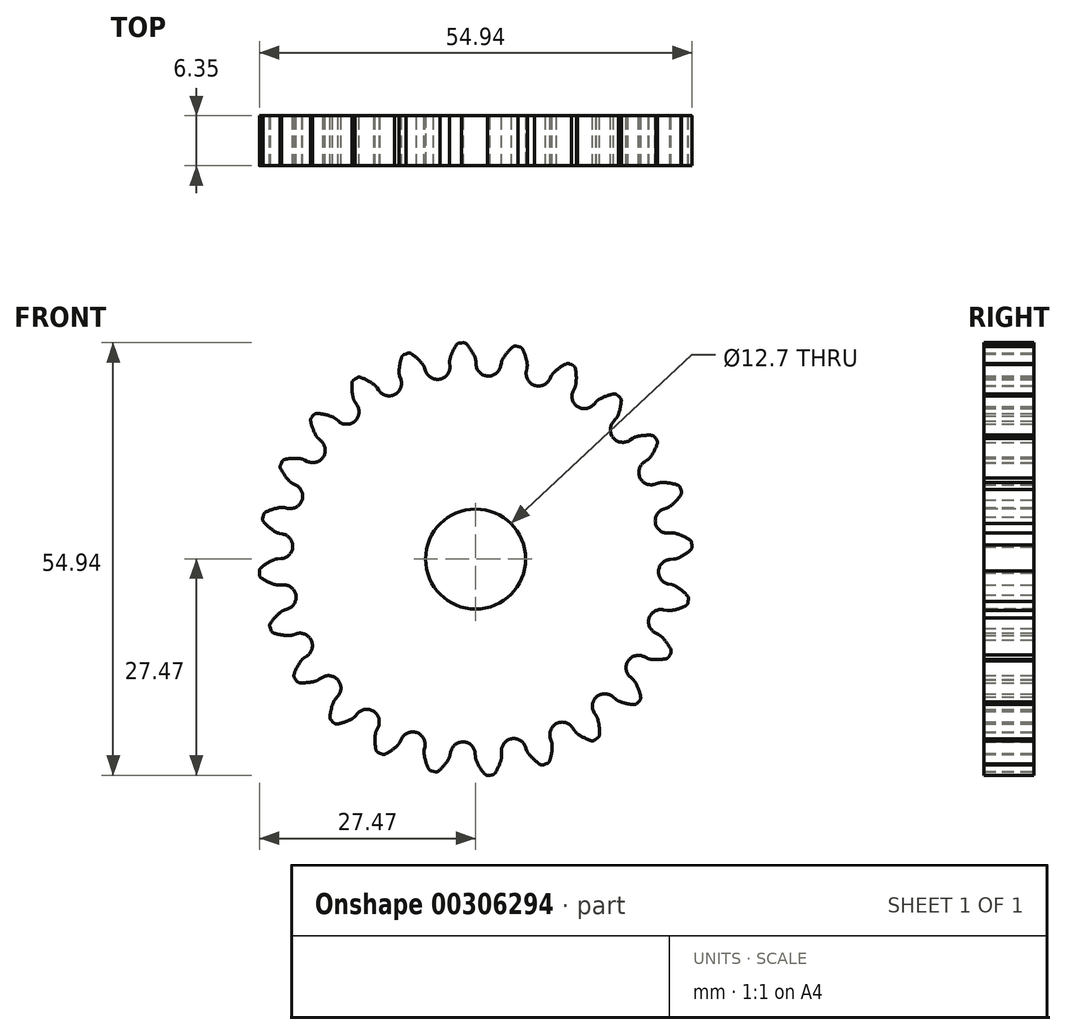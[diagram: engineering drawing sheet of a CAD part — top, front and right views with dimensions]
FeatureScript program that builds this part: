
annotation { "Feature Type Name" : "Feature", "Feature Type Description" : "" }
export const myFeature = defineFeature(function(context is Context, id is Id, definition is map)
    precondition{}
    {
        {
            var Q0;
            Q0=qCreatedBy(makeId("Front.planeOp"),FACE);
            var sketch = newSketch(context, id + "F0", { "sketchPlane" : qUnion([Q0])});
            skArc(sketch, "E0.trimOffspring", {"start": v(-0.1, 25.68) * mm, "mid": v(-0.56, 26.53) * mm, "end": v(-1.14, 27.3) * mm});
            skLineSegment(sketch, "E1", {"start": v(-1.55, 27.47) * mm, "end": v(-1.8, 27.46) * mm});
            skLineSegment(sketch, "E2.MirrorCS", {"start": v(-2.05, 27.44) * mm, "end": v(-1.8, 27.46) * mm});
            skArc(sketch, "E3.MirrorCS", {"start": v(-3.24, 25.47) * mm, "mid": v(-2.9, 26.38) * mm, "end": v(-2.43, 27.22) * mm});
            skLineSegment(sketch, "E4", {"start": v(0.02, 25.14) * mm, "end": v(0.05, 24.72) * mm});
            skLineSegment(sketch, "E5.MirrorCS", {"start": v(-3.3, 24.92) * mm, "end": v(-3.28, 24.5) * mm});
            skPoint(sketch, "E6.visualSharp", {"position": v(0.14, 23.28) * mm});
            skArc(sketch, "E6.filletArc", {"start": v(0.05, 24.72) * mm, "mid": v(0.51, 23.7) * mm, "end": v(1.54, 23.23) * mm});
            skPoint(sketch, "E7.visualSharp", {"position": v(-3.18, 23.06) * mm});
            skArc(sketch, "E7.filletArc", {"start": v(-4.56, 22.83) * mm, "mid": v(-3.6, 23.43) * mm, "end": v(-3.28, 24.5) * mm});
            skPoint(sketch, "E8.visualSharp", {"position": v(-3.32, 25.18) * mm});
            skArc(sketch, "E8.filletArc", {"start": v(-3.24, 25.47) * mm, "mid": v(-3.3, 25.2) * mm, "end": v(-3.3, 24.92) * mm});
            skPoint(sketch, "E9.visualSharp", {"position": v(0, 25.4) * mm});
            skArc(sketch, "E9.filletArc", {"start": v(0.02, 25.14) * mm, "mid": v(-0.02, 25.42) * mm, "end": v(-0.1, 25.68) * mm});
            skPoint(sketch, "E10.visualSharp", {"position": v(-2.3, 27.42) * mm});
            skArc(sketch, "E10.filletArc", {"start": v(-2.05, 27.44) * mm, "mid": v(-2.27, 27.37) * mm, "end": v(-2.43, 27.22) * mm});
            skPoint(sketch, "E11.visualSharp", {"position": v(-1.3, 27.49) * mm});
            skArc(sketch, "E11.filletArc", {"start": v(-1.14, 27.3) * mm, "mid": v(-1.32, 27.43) * mm, "end": v(-1.55, 27.47) * mm});
            skArc(sketch, "E12.1.0", {"start": v(-9.73, 23.77) * mm, "mid": v(-9.63, 24.73) * mm, "end": v(-9.4, 25.66) * mm});
            skPoint(sketch, "E12.1.1", {"position": v(-9.3, 25.9) * mm});
            skPoint(sketch, "E12.1.2", {"position": v(-8.38, 26.21) * mm});
            skArc(sketch, "E12.1.3", {"start": v(-10.31, 20.87) * mm, "mid": v(-9.54, 21.7) * mm, "end": v(-9.5, 22.82) * mm});
            skPoint(sketch, "E12.1.4", {"position": v(-5.89, 22.53) * mm});
            skPoint(sketch, "E12.1.5", {"position": v(-9.04, 21.46) * mm});
            skPoint(sketch, "E12.1.6", {"position": v(-9.73, 23.46) * mm});
            skArc(sketch, "E12.1.7", {"start": v(-6.35, 23.9) * mm, "mid": v(-5.64, 23.02) * mm, "end": v(-4.52, 22.84) * mm});
            skPoint(sketch, "E12.1.8", {"position": v(-6.57, 24.54) * mm});
            skArc(sketch, "E12.1.9", {"start": v(-6.75, 24.78) * mm, "mid": v(-7.41, 25.48) * mm, "end": v(-8.17, 26.08) * mm});
            skLineSegment(sketch, "E12.1.10", {"start": v(-9.64, 23.22) * mm, "end": v(-9.5, 22.82) * mm});
            skArc(sketch, "E12.1.11", {"start": v(-8.17, 26.08) * mm, "mid": v(-8.38, 26.16) * mm, "end": v(-8.6, 26.14) * mm});
            skArc(sketch, "E12.1.12", {"start": v(-6.48, 24.29) * mm, "mid": v(-6.6, 24.54) * mm, "end": v(-6.75, 24.78) * mm});
            skLineSegment(sketch, "E12.1.13", {"start": v(-6.48, 24.29) * mm, "end": v(-6.35, 23.9) * mm});
            skLineSegment(sketch, "E12.1.14", {"start": v(-8.6, 26.14) * mm, "end": v(-8.85, 26.06) * mm});
            skArc(sketch, "E12.1.15", {"start": v(-9.73, 23.77) * mm, "mid": v(-9.7, 23.49) * mm, "end": v(-9.64, 23.22) * mm});
            skLineSegment(sketch, "E12.1.16", {"start": v(-9.08, 25.97) * mm, "end": v(-8.85, 26.06) * mm});
            skArc(sketch, "E12.1.17", {"start": v(-9.08, 25.97) * mm, "mid": v(-9.28, 25.85) * mm, "end": v(-9.4, 25.66) * mm});
            skArc(sketch, "E12.2.0", {"start": v(-15.55, 20.44) * mm, "mid": v(-15.7, 21.4) * mm, "end": v(-15.71, 22.35) * mm});
            skPoint(sketch, "E12.2.1", {"position": v(-15.7, 22.6) * mm});
            skPoint(sketch, "E12.2.2", {"position": v(-14.88, 23.15) * mm});
            skArc(sketch, "E12.2.3", {"start": v(-15.37, 17.5) * mm, "mid": v(-14.83, 18.49) * mm, "end": v(-15.1, 19.58) * mm});
            skPoint(sketch, "E12.2.4", {"position": v(-11.52, 20.24) * mm});
            skPoint(sketch, "E12.2.5", {"position": v(-14.29, 18.38) * mm});
            skPoint(sketch, "E12.2.6", {"position": v(-15.47, 20.15) * mm});
            skArc(sketch, "E12.2.7", {"start": v(-12.32, 21.44) * mm, "mid": v(-11.4, 20.78) * mm, "end": v(-10.28, 20.9) * mm});
            skPoint(sketch, "E12.2.8", {"position": v(-12.7, 22) * mm});
            skArc(sketch, "E12.2.9", {"start": v(-12.93, 22.18) * mm, "mid": v(-13.75, 22.7) * mm, "end": v(-14.64, 23.07) * mm});
            skLineSegment(sketch, "E12.2.10", {"start": v(-15.32, 19.93) * mm, "end": v(-15.1, 19.58) * mm});
            skArc(sketch, "E12.2.11", {"start": v(-14.64, 23.07) * mm, "mid": v(-14.86, 23.1) * mm, "end": v(-15.08, 23.02) * mm});
            skArc(sketch, "E12.2.12", {"start": v(-12.55, 21.78) * mm, "mid": v(-12.72, 22) * mm, "end": v(-12.93, 22.18) * mm});
            skLineSegment(sketch, "E12.2.13", {"start": v(-12.55, 21.78) * mm, "end": v(-12.32, 21.44) * mm});
            skLineSegment(sketch, "E12.2.14", {"start": v(-15.08, 23.02) * mm, "end": v(-15.29, 22.88) * mm});
            skArc(sketch, "E12.2.15", {"start": v(-15.55, 20.44) * mm, "mid": v(-15.46, 20.18) * mm, "end": v(-15.32, 19.93) * mm});
            skLineSegment(sketch, "E12.2.16", {"start": v(-15.5, 22.74) * mm, "end": v(-15.29, 22.88) * mm});
            skArc(sketch, "E12.2.17", {"start": v(-15.5, 22.74) * mm, "mid": v(-15.65, 22.57) * mm, "end": v(-15.71, 22.35) * mm});
            skPoint(sketch, "E12.center", {"position": v(0, 0) * mm});
            skPoint(sketch, "E13.4.3.0", {"position": v(-21, 17.77) * mm});
            skPoint(sketch, "E13.5.3.0", {"position": v(-20.36, 18.51) * mm});
            skArc(sketch, "E13.6.3.0", {"start": v(-19.37, 12.92) * mm, "mid": v(-19.11, 14.02) * mm, "end": v(-19.65, 15.01) * mm});
            skPoint(sketch, "E13.10.3.0", {"position": v(-16.36, 16.57) * mm});
            skPoint(sketch, "E13.11.3.0", {"position": v(-18.56, 14.06) * mm});
            skPoint(sketch, "E13.12.3.0", {"position": v(-20.15, 15.46) * mm});
            skArc(sketch, "E13.13.3.0", {"start": v(-17.45, 17.52) * mm, "mid": v(-16.4, 17.12) * mm, "end": v(-15.34, 17.52) * mm});
            skPoint(sketch, "E13.17.3.0", {"position": v(-17.96, 17.96) * mm});
            skArc(sketch, "E13.18.3.0", {"start": v(-18.24, 18.08) * mm, "mid": v(-19.16, 18.36) * mm, "end": v(-20.11, 18.5) * mm});
            skArc(sketch, "E13.19.3.0", {"start": v(-20.3, 15.72) * mm, "mid": v(-20.7, 16.6) * mm, "end": v(-20.97, 17.52) * mm});
            skLineSegment(sketch, "E13.22.3.0", {"start": v(-19.96, 15.29) * mm, "end": v(-19.65, 15.01) * mm});
            skArc(sketch, "E13.25.3.0", {"start": v(-20.11, 18.5) * mm, "mid": v(-20.34, 18.46) * mm, "end": v(-20.52, 18.33) * mm});
            skArc(sketch, "E13.29.3.0", {"start": v(-17.76, 17.8) * mm, "mid": v(-17.99, 17.96) * mm, "end": v(-18.24, 18.08) * mm});
            skLineSegment(sketch, "E13.33.3.0", {"start": v(-17.76, 17.8) * mm, "end": v(-17.45, 17.52) * mm});
            skLineSegment(sketch, "E13.36.3.0", {"start": v(-20.52, 18.33) * mm, "end": v(-20.7, 18.15) * mm});
            skArc(sketch, "E13.39.3.0", {"start": v(-20.3, 15.72) * mm, "mid": v(-20.15, 15.49) * mm, "end": v(-19.96, 15.29) * mm});
            skLineSegment(sketch, "E13.43.3.0", {"start": v(-20.85, 17.95) * mm, "end": v(-20.7, 18.15) * mm});
            skArc(sketch, "E13.46.3.0", {"start": v(-20.85, 17.95) * mm, "mid": v(-20.96, 17.75) * mm, "end": v(-20.97, 17.52) * mm});
            skPoint(sketch, "E13.4.4.0", {"position": v(-24.9, 11.73) * mm});
            skPoint(sketch, "E13.5.4.0", {"position": v(-24.46, 12.6) * mm});
            skArc(sketch, "E13.6.4.0", {"start": v(-22.05, 7.47) * mm, "mid": v(-22.1, 8.6) * mm, "end": v(-22.86, 9.42) * mm});
            skPoint(sketch, "E13.10.4.0", {"position": v(-20.1, 11.77) * mm});
            skPoint(sketch, "E13.11.4.0", {"position": v(-21.57, 8.78) * mm});
            skPoint(sketch, "E13.12.4.0", {"position": v(-23.47, 9.71) * mm});
            skArc(sketch, "E13.13.4.0", {"start": v(-21.39, 12.4) * mm, "mid": v(-20.27, 12.3) * mm, "end": v(-19.35, 12.95) * mm});
            skPoint(sketch, "E13.17.4.0", {"position": v(-22, 12.7) * mm});
            skArc(sketch, "E13.18.4.0", {"start": v(-22.3, 12.74) * mm, "mid": v(-23.26, 12.78) * mm, "end": v(-24.21, 12.66) * mm});
            skArc(sketch, "E13.19.4.0", {"start": v(-23.68, 9.93) * mm, "mid": v(-24.3, 10.67) * mm, "end": v(-24.79, 11.5) * mm});
            skLineSegment(sketch, "E13.22.4.0", {"start": v(-23.23, 9.6) * mm, "end": v(-22.86, 9.42) * mm});
            skArc(sketch, "E13.25.4.0", {"start": v(-24.21, 12.66) * mm, "mid": v(-24.42, 12.57) * mm, "end": v(-24.57, 12.4) * mm});
            skArc(sketch, "E13.29.4.0", {"start": v(-21.76, 12.59) * mm, "mid": v(-22.02, 12.7) * mm, "end": v(-22.3, 12.74) * mm});
            skLineSegment(sketch, "E13.33.4.0", {"start": v(-21.76, 12.59) * mm, "end": v(-21.39, 12.4) * mm});
            skLineSegment(sketch, "E13.36.4.0", {"start": v(-24.57, 12.4) * mm, "end": v(-24.68, 12.17) * mm});
            skArc(sketch, "E13.39.4.0", {"start": v(-23.68, 9.93) * mm, "mid": v(-23.47, 9.74) * mm, "end": v(-23.23, 9.6) * mm});
            skLineSegment(sketch, "E13.43.4.0", {"start": v(-24.8, 11.94) * mm, "end": v(-24.68, 12.17) * mm});
            skArc(sketch, "E13.46.4.0", {"start": v(-24.8, 11.94) * mm, "mid": v(-24.84, 11.72) * mm, "end": v(-24.79, 11.5) * mm});
            skPoint(sketch, "E13.4.5.0", {"position": v(-27.08, 4.88) * mm});
            skPoint(sketch, "E13.5.5.0", {"position": v(-26.89, 5.85) * mm});
            skArc(sketch, "E13.6.5.0", {"start": v(-23.23, 1.5) * mm, "mid": v(-23.56, 2.58) * mm, "end": v(-24.52, 3.18) * mm});
            skPoint(sketch, "E13.10.5.0", {"position": v(-22.45, 6.17) * mm});
            skPoint(sketch, "E13.11.5.0", {"position": v(-23.1, 2.9) * mm});
            skPoint(sketch, "E13.12.5.0", {"position": v(-25.18, 3.3) * mm});
            skArc(sketch, "E13.13.5.0", {"start": v(-23.87, 6.45) * mm, "mid": v(-22.76, 6.63) * mm, "end": v(-22.04, 7.5) * mm});
            skPoint(sketch, "E13.17.5.0", {"position": v(-24.53, 6.58) * mm});
            skArc(sketch, "E13.18.5.0", {"start": v(-24.83, 6.54) * mm, "mid": v(-25.77, 6.32) * mm, "end": v(-26.67, 5.96) * mm});
            skArc(sketch, "E13.19.5.0", {"start": v(-25.45, 3.46) * mm, "mid": v(-26.23, 4.02) * mm, "end": v(-26.92, 4.7) * mm});
            skLineSegment(sketch, "E13.22.5.0", {"start": v(-24.93, 3.26) * mm, "end": v(-24.52, 3.18) * mm});
            skArc(sketch, "E13.25.5.0", {"start": v(-26.67, 5.96) * mm, "mid": v(-26.84, 5.82) * mm, "end": v(-26.94, 5.62) * mm});
            skArc(sketch, "E13.29.5.0", {"start": v(-24.28, 6.53) * mm, "mid": v(-24.55, 6.56) * mm, "end": v(-24.83, 6.54) * mm});
            skLineSegment(sketch, "E13.33.5.0", {"start": v(-24.28, 6.53) * mm, "end": v(-23.87, 6.45) * mm});
            skLineSegment(sketch, "E13.36.5.0", {"start": v(-26.94, 5.62) * mm, "end": v(-27, 5.37) * mm});
            skArc(sketch, "E13.39.5.0", {"start": v(-25.45, 3.46) * mm, "mid": v(-25.2, 3.34) * mm, "end": v(-24.93, 3.26) * mm});
            skLineSegment(sketch, "E13.43.5.0", {"start": v(-27.04, 5.12) * mm, "end": v(-27, 5.37) * mm});
            skArc(sketch, "E13.46.5.0", {"start": v(-27.04, 5.12) * mm, "mid": v(-27.03, 4.9) * mm, "end": v(-26.92, 4.7) * mm});
            skPoint(sketch, "E13.4.6.0", {"position": v(-27.42, -2.3) * mm});
            skPoint(sketch, "E13.5.6.0", {"position": v(-27.49, -1.3) * mm});
            skArc(sketch, "E13.6.6.0", {"start": v(-22.83, -4.56) * mm, "mid": v(-23.43, -3.6) * mm, "end": v(-24.5, -3.28) * mm});
            skPoint(sketch, "E13.10.6.0", {"position": v(-23.28, 0.14) * mm});
            skPoint(sketch, "E13.11.6.0", {"position": v(-23.06, -3.18) * mm});
            skPoint(sketch, "E13.12.6.0", {"position": v(-25.18, -3.32) * mm});
            skArc(sketch, "E13.13.6.0", {"start": v(-24.72, 0.05) * mm, "mid": v(-23.7, 0.51) * mm, "end": v(-23.23, 1.54) * mm});
            skPoint(sketch, "E13.17.6.0", {"position": v(-25.4, 0) * mm});
            skArc(sketch, "E13.18.6.0", {"start": v(-25.68, -0.1) * mm, "mid": v(-26.53, -0.56) * mm, "end": v(-27.3, -1.14) * mm});
            skArc(sketch, "E13.19.6.0", {"start": v(-25.47, -3.24) * mm, "mid": v(-26.38, -2.9) * mm, "end": v(-27.22, -2.43) * mm});
            skLineSegment(sketch, "E13.22.6.0", {"start": v(-24.92, -3.3) * mm, "end": v(-24.5, -3.28) * mm});
            skArc(sketch, "E13.25.6.0", {"start": v(-27.3, -1.14) * mm, "mid": v(-27.43, -1.32) * mm, "end": v(-27.47, -1.55) * mm});
            skArc(sketch, "E13.29.6.0", {"start": v(-25.14, 0.02) * mm, "mid": v(-25.42, -0.02) * mm, "end": v(-25.68, -0.1) * mm});
            skLineSegment(sketch, "E13.33.6.0", {"start": v(-25.14, 0.02) * mm, "end": v(-24.72, 0.05) * mm});
            skLineSegment(sketch, "E13.36.6.0", {"start": v(-27.47, -1.55) * mm, "end": v(-27.46, -1.8) * mm});
            skArc(sketch, "E13.39.6.0", {"start": v(-25.47, -3.24) * mm, "mid": v(-25.2, -3.3) * mm, "end": v(-24.92, -3.3) * mm});
            skLineSegment(sketch, "E13.43.6.0", {"start": v(-27.44, -2.05) * mm, "end": v(-27.46, -1.8) * mm});
            skArc(sketch, "E13.46.6.0", {"start": v(-27.44, -2.05) * mm, "mid": v(-27.37, -2.27) * mm, "end": v(-27.22, -2.43) * mm});
            skPoint(sketch, "E13.4.7.0", {"position": v(-25.9, -9.3) * mm});
            skPoint(sketch, "E13.5.7.0", {"position": v(-26.21, -8.38) * mm});
            skArc(sketch, "E13.6.7.0", {"start": v(-20.87, -10.31) * mm, "mid": v(-21.7, -9.54) * mm, "end": v(-22.82, -9.5) * mm});
            skPoint(sketch, "E13.10.7.0", {"position": v(-22.53, -5.89) * mm});
            skPoint(sketch, "E13.11.7.0", {"position": v(-21.46, -9.04) * mm});
            skPoint(sketch, "E13.12.7.0", {"position": v(-23.46, -9.73) * mm});
            skArc(sketch, "E13.13.7.0", {"start": v(-23.9, -6.35) * mm, "mid": v(-23.02, -5.64) * mm, "end": v(-22.84, -4.52) * mm});
            skPoint(sketch, "E13.17.7.0", {"position": v(-24.54, -6.57) * mm});
            skArc(sketch, "E13.18.7.0", {"start": v(-24.78, -6.75) * mm, "mid": v(-25.48, -7.41) * mm, "end": v(-26.08, -8.17) * mm});
            skArc(sketch, "E13.19.7.0", {"start": v(-23.77, -9.73) * mm, "mid": v(-24.73, -9.63) * mm, "end": v(-25.66, -9.4) * mm});
            skLineSegment(sketch, "E13.22.7.0", {"start": v(-23.22, -9.64) * mm, "end": v(-22.82, -9.5) * mm});
            skArc(sketch, "E13.25.7.0", {"start": v(-26.08, -8.17) * mm, "mid": v(-26.16, -8.38) * mm, "end": v(-26.14, -8.6) * mm});
            skArc(sketch, "E13.29.7.0", {"start": v(-24.29, -6.48) * mm, "mid": v(-24.54, -6.6) * mm, "end": v(-24.78, -6.75) * mm});
            skLineSegment(sketch, "E13.33.7.0", {"start": v(-24.29, -6.48) * mm, "end": v(-23.9, -6.35) * mm});
            skLineSegment(sketch, "E13.36.7.0", {"start": v(-26.14, -8.6) * mm, "end": v(-26.06, -8.85) * mm});
            skArc(sketch, "E13.39.7.0", {"start": v(-23.77, -9.73) * mm, "mid": v(-23.49, -9.7) * mm, "end": v(-23.22, -9.64) * mm});
            skLineSegment(sketch, "E13.43.7.0", {"start": v(-25.97, -9.08) * mm, "end": v(-26.06, -8.85) * mm});
            skArc(sketch, "E13.46.7.0", {"start": v(-25.97, -9.08) * mm, "mid": v(-25.85, -9.28) * mm, "end": v(-25.66, -9.4) * mm});
            skPoint(sketch, "E13.4.8.0", {"position": v(-22.6, -15.7) * mm});
            skPoint(sketch, "E13.5.8.0", {"position": v(-23.15, -14.88) * mm});
            skArc(sketch, "E13.6.8.0", {"start": v(-17.5, -15.37) * mm, "mid": v(-18.49, -14.83) * mm, "end": v(-19.58, -15.1) * mm});
            skPoint(sketch, "E13.10.8.0", {"position": v(-20.24, -11.52) * mm});
            skPoint(sketch, "E13.11.8.0", {"position": v(-18.38, -14.29) * mm});
            skPoint(sketch, "E13.12.8.0", {"position": v(-20.15, -15.47) * mm});
            skArc(sketch, "E13.13.8.0", {"start": v(-21.44, -12.32) * mm, "mid": v(-20.78, -11.4) * mm, "end": v(-20.9, -10.28) * mm});
            skPoint(sketch, "E13.17.8.0", {"position": v(-22, -12.7) * mm});
            skArc(sketch, "E13.18.8.0", {"start": v(-22.18, -12.93) * mm, "mid": v(-22.7, -13.75) * mm, "end": v(-23.07, -14.64) * mm});
            skArc(sketch, "E13.19.8.0", {"start": v(-20.44, -15.55) * mm, "mid": v(-21.4, -15.7) * mm, "end": v(-22.35, -15.71) * mm});
            skLineSegment(sketch, "E13.22.8.0", {"start": v(-19.93, -15.32) * mm, "end": v(-19.58, -15.1) * mm});
            skArc(sketch, "E13.25.8.0", {"start": v(-23.07, -14.64) * mm, "mid": v(-23.1, -14.86) * mm, "end": v(-23.02, -15.08) * mm});
            skArc(sketch, "E13.29.8.0", {"start": v(-21.78, -12.55) * mm, "mid": v(-22, -12.72) * mm, "end": v(-22.18, -12.93) * mm});
            skLineSegment(sketch, "E13.33.8.0", {"start": v(-21.78, -12.55) * mm, "end": v(-21.44, -12.32) * mm});
            skLineSegment(sketch, "E13.36.8.0", {"start": v(-23.02, -15.08) * mm, "end": v(-22.88, -15.29) * mm});
            skArc(sketch, "E13.39.8.0", {"start": v(-20.44, -15.55) * mm, "mid": v(-20.18, -15.46) * mm, "end": v(-19.93, -15.32) * mm});
            skLineSegment(sketch, "E13.43.8.0", {"start": v(-22.74, -15.5) * mm, "end": v(-22.88, -15.29) * mm});
            skArc(sketch, "E13.46.8.0", {"start": v(-22.74, -15.5) * mm, "mid": v(-22.57, -15.65) * mm, "end": v(-22.35, -15.71) * mm});
            skPoint(sketch, "E13.4.9.0", {"position": v(-17.77, -21) * mm});
            skPoint(sketch, "E13.5.9.0", {"position": v(-18.51, -20.36) * mm});
            skArc(sketch, "E13.6.9.0", {"start": v(-12.92, -19.37) * mm, "mid": v(-14.02, -19.11) * mm, "end": v(-15.01, -19.65) * mm});
            skPoint(sketch, "E13.10.9.0", {"position": v(-16.57, -16.36) * mm});
            skPoint(sketch, "E13.11.9.0", {"position": v(-14.06, -18.56) * mm});
            skPoint(sketch, "E13.12.9.0", {"position": v(-15.46, -20.15) * mm});
            skArc(sketch, "E13.13.9.0", {"start": v(-17.52, -17.45) * mm, "mid": v(-17.12, -16.4) * mm, "end": v(-17.52, -15.34) * mm});
            skPoint(sketch, "E13.17.9.0", {"position": v(-17.96, -17.96) * mm});
            skArc(sketch, "E13.18.9.0", {"start": v(-18.08, -18.24) * mm, "mid": v(-18.36, -19.16) * mm, "end": v(-18.5, -20.11) * mm});
            skArc(sketch, "E13.19.9.0", {"start": v(-15.72, -20.3) * mm, "mid": v(-16.6, -20.7) * mm, "end": v(-17.52, -20.97) * mm});
            skLineSegment(sketch, "E13.22.9.0", {"start": v(-15.29, -19.96) * mm, "end": v(-15.01, -19.65) * mm});
            skArc(sketch, "E13.25.9.0", {"start": v(-18.5, -20.11) * mm, "mid": v(-18.46, -20.34) * mm, "end": v(-18.33, -20.52) * mm});
            skArc(sketch, "E13.29.9.0", {"start": v(-17.8, -17.76) * mm, "mid": v(-17.96, -17.99) * mm, "end": v(-18.08, -18.24) * mm});
            skLineSegment(sketch, "E13.33.9.0", {"start": v(-17.8, -17.76) * mm, "end": v(-17.52, -17.45) * mm});
            skLineSegment(sketch, "E13.36.9.0", {"start": v(-18.33, -20.52) * mm, "end": v(-18.15, -20.7) * mm});
            skArc(sketch, "E13.39.9.0", {"start": v(-15.72, -20.3) * mm, "mid": v(-15.49, -20.15) * mm, "end": v(-15.29, -19.96) * mm});
            skLineSegment(sketch, "E13.43.9.0", {"start": v(-17.95, -20.85) * mm, "end": v(-18.15, -20.7) * mm});
            skArc(sketch, "E13.46.9.0", {"start": v(-17.95, -20.85) * mm, "mid": v(-17.75, -20.96) * mm, "end": v(-17.52, -20.97) * mm});
            skPoint(sketch, "E13.4.10.0", {"position": v(-11.73, -24.9) * mm});
            skPoint(sketch, "E13.5.10.0", {"position": v(-12.6, -24.46) * mm});
            skArc(sketch, "E13.6.10.0", {"start": v(-7.47, -22.05) * mm, "mid": v(-8.6, -22.1) * mm, "end": v(-9.42, -22.86) * mm});
            skPoint(sketch, "E13.10.10.0", {"position": v(-11.77, -20.1) * mm});
            skPoint(sketch, "E13.11.10.0", {"position": v(-8.78, -21.57) * mm});
            skPoint(sketch, "E13.12.10.0", {"position": v(-9.71, -23.47) * mm});
            skArc(sketch, "E13.13.10.0", {"start": v(-12.4, -21.39) * mm, "mid": v(-12.3, -20.27) * mm, "end": v(-12.95, -19.35) * mm});
            skPoint(sketch, "E13.17.10.0", {"position": v(-12.7, -22) * mm});
            skArc(sketch, "E13.18.10.0", {"start": v(-12.74, -22.3) * mm, "mid": v(-12.78, -23.26) * mm, "end": v(-12.66, -24.21) * mm});
            skArc(sketch, "E13.19.10.0", {"start": v(-9.93, -23.68) * mm, "mid": v(-10.67, -24.3) * mm, "end": v(-11.5, -24.79) * mm});
            skLineSegment(sketch, "E13.22.10.0", {"start": v(-9.6, -23.23) * mm, "end": v(-9.42, -22.86) * mm});
            skArc(sketch, "E13.25.10.0", {"start": v(-12.66, -24.21) * mm, "mid": v(-12.57, -24.42) * mm, "end": v(-12.4, -24.57) * mm});
            skArc(sketch, "E13.29.10.0", {"start": v(-12.59, -21.76) * mm, "mid": v(-12.7, -22.02) * mm, "end": v(-12.74, -22.3) * mm});
            skLineSegment(sketch, "E13.33.10.0", {"start": v(-12.59, -21.76) * mm, "end": v(-12.4, -21.39) * mm});
            skLineSegment(sketch, "E13.36.10.0", {"start": v(-12.4, -24.57) * mm, "end": v(-12.17, -24.68) * mm});
            skArc(sketch, "E13.39.10.0", {"start": v(-9.93, -23.68) * mm, "mid": v(-9.74, -23.47) * mm, "end": v(-9.6, -23.23) * mm});
            skLineSegment(sketch, "E13.43.10.0", {"start": v(-11.94, -24.8) * mm, "end": v(-12.17, -24.68) * mm});
            skArc(sketch, "E13.46.10.0", {"start": v(-11.94, -24.8) * mm, "mid": v(-11.72, -24.84) * mm, "end": v(-11.5, -24.79) * mm});
            skPoint(sketch, "E13.4.11.0", {"position": v(-4.88, -27.08) * mm});
            skPoint(sketch, "E13.5.11.0", {"position": v(-5.85, -26.89) * mm});
            skArc(sketch, "E13.6.11.0", {"start": v(-1.5, -23.23) * mm, "mid": v(-2.58, -23.56) * mm, "end": v(-3.18, -24.52) * mm});
            skPoint(sketch, "E13.10.11.0", {"position": v(-6.17, -22.45) * mm});
            skPoint(sketch, "E13.11.11.0", {"position": v(-2.9, -23.1) * mm});
            skPoint(sketch, "E13.12.11.0", {"position": v(-3.3, -25.18) * mm});
            skArc(sketch, "E13.13.11.0", {"start": v(-6.45, -23.87) * mm, "mid": v(-6.63, -22.76) * mm, "end": v(-7.5, -22.04) * mm});
            skPoint(sketch, "E13.17.11.0", {"position": v(-6.58, -24.53) * mm});
            skArc(sketch, "E13.18.11.0", {"start": v(-6.54, -24.83) * mm, "mid": v(-6.32, -25.77) * mm, "end": v(-5.96, -26.67) * mm});
            skArc(sketch, "E13.19.11.0", {"start": v(-3.46, -25.45) * mm, "mid": v(-4.02, -26.23) * mm, "end": v(-4.7, -26.92) * mm});
            skLineSegment(sketch, "E13.22.11.0", {"start": v(-3.26, -24.93) * mm, "end": v(-3.18, -24.52) * mm});
            skArc(sketch, "E13.25.11.0", {"start": v(-5.96, -26.67) * mm, "mid": v(-5.82, -26.84) * mm, "end": v(-5.62, -26.94) * mm});
            skArc(sketch, "E13.29.11.0", {"start": v(-6.53, -24.28) * mm, "mid": v(-6.56, -24.55) * mm, "end": v(-6.54, -24.83) * mm});
            skLineSegment(sketch, "E13.33.11.0", {"start": v(-6.53, -24.28) * mm, "end": v(-6.45, -23.87) * mm});
            skLineSegment(sketch, "E13.36.11.0", {"start": v(-5.62, -26.94) * mm, "end": v(-5.37, -27) * mm});
            skArc(sketch, "E13.39.11.0", {"start": v(-3.46, -25.45) * mm, "mid": v(-3.34, -25.2) * mm, "end": v(-3.26, -24.93) * mm});
            skLineSegment(sketch, "E13.43.11.0", {"start": v(-5.12, -27.04) * mm, "end": v(-5.37, -27) * mm});
            skArc(sketch, "E13.46.11.0", {"start": v(-5.12, -27.04) * mm, "mid": v(-4.9, -27.03) * mm, "end": v(-4.7, -26.92) * mm});
            skPoint(sketch, "E13.4.12.0", {"position": v(2.3, -27.42) * mm});
            skPoint(sketch, "E13.5.12.0", {"position": v(1.3, -27.49) * mm});
            skArc(sketch, "E13.6.12.0", {"start": v(4.56, -22.83) * mm, "mid": v(3.6, -23.43) * mm, "end": v(3.28, -24.5) * mm});
            skPoint(sketch, "E13.10.12.0", {"position": v(-0.14, -23.28) * mm});
            skPoint(sketch, "E13.11.12.0", {"position": v(3.18, -23.06) * mm});
            skPoint(sketch, "E13.12.12.0", {"position": v(3.32, -25.18) * mm});
            skArc(sketch, "E13.13.12.0", {"start": v(-0.05, -24.72) * mm, "mid": v(-0.51, -23.7) * mm, "end": v(-1.54, -23.23) * mm});
            skPoint(sketch, "E13.17.12.0", {"position": v(0, -25.4) * mm});
            skArc(sketch, "E13.18.12.0", {"start": v(0.1, -25.68) * mm, "mid": v(0.56, -26.53) * mm, "end": v(1.14, -27.3) * mm});
            skArc(sketch, "E13.19.12.0", {"start": v(3.24, -25.47) * mm, "mid": v(2.9, -26.38) * mm, "end": v(2.43, -27.22) * mm});
            skLineSegment(sketch, "E13.22.12.0", {"start": v(3.3, -24.92) * mm, "end": v(3.28, -24.5) * mm});
            skArc(sketch, "E13.25.12.0", {"start": v(1.14, -27.3) * mm, "mid": v(1.32, -27.43) * mm, "end": v(1.55, -27.47) * mm});
            skArc(sketch, "E13.29.12.0", {"start": v(-0.02, -25.14) * mm, "mid": v(0.02, -25.42) * mm, "end": v(0.1, -25.68) * mm});
            skLineSegment(sketch, "E13.33.12.0", {"start": v(-0.02, -25.14) * mm, "end": v(-0.05, -24.72) * mm});
            skLineSegment(sketch, "E13.36.12.0", {"start": v(1.55, -27.47) * mm, "end": v(1.8, -27.46) * mm});
            skArc(sketch, "E13.39.12.0", {"start": v(3.24, -25.47) * mm, "mid": v(3.3, -25.2) * mm, "end": v(3.3, -24.92) * mm});
            skLineSegment(sketch, "E13.43.12.0", {"start": v(2.05, -27.44) * mm, "end": v(1.8, -27.46) * mm});
            skArc(sketch, "E13.46.12.0", {"start": v(2.05, -27.44) * mm, "mid": v(2.27, -27.37) * mm, "end": v(2.43, -27.22) * mm});
            skPoint(sketch, "E13.4.13.0", {"position": v(9.3, -25.9) * mm});
            skPoint(sketch, "E13.5.13.0", {"position": v(8.38, -26.21) * mm});
            skArc(sketch, "E13.6.13.0", {"start": v(10.31, -20.87) * mm, "mid": v(9.54, -21.7) * mm, "end": v(9.5, -22.82) * mm});
            skPoint(sketch, "E13.10.13.0", {"position": v(5.89, -22.53) * mm});
            skPoint(sketch, "E13.11.13.0", {"position": v(9.04, -21.46) * mm});
            skPoint(sketch, "E13.12.13.0", {"position": v(9.73, -23.46) * mm});
            skArc(sketch, "E13.13.13.0", {"start": v(6.35, -23.9) * mm, "mid": v(5.64, -23.02) * mm, "end": v(4.52, -22.84) * mm});
            skPoint(sketch, "E13.17.13.0", {"position": v(6.57, -24.54) * mm});
            skArc(sketch, "E13.18.13.0", {"start": v(6.75, -24.78) * mm, "mid": v(7.41, -25.48) * mm, "end": v(8.17, -26.08) * mm});
            skArc(sketch, "E13.19.13.0", {"start": v(9.73, -23.77) * mm, "mid": v(9.63, -24.73) * mm, "end": v(9.4, -25.66) * mm});
            skLineSegment(sketch, "E13.22.13.0", {"start": v(9.64, -23.22) * mm, "end": v(9.5, -22.82) * mm});
            skArc(sketch, "E13.25.13.0", {"start": v(8.17, -26.08) * mm, "mid": v(8.38, -26.16) * mm, "end": v(8.6, -26.14) * mm});
            skArc(sketch, "E13.29.13.0", {"start": v(6.48, -24.29) * mm, "mid": v(6.6, -24.54) * mm, "end": v(6.75, -24.78) * mm});
            skLineSegment(sketch, "E13.33.13.0", {"start": v(6.48, -24.29) * mm, "end": v(6.35, -23.9) * mm});
            skLineSegment(sketch, "E13.36.13.0", {"start": v(8.6, -26.14) * mm, "end": v(8.85, -26.06) * mm});
            skArc(sketch, "E13.39.13.0", {"start": v(9.73, -23.77) * mm, "mid": v(9.7, -23.49) * mm, "end": v(9.64, -23.22) * mm});
            skLineSegment(sketch, "E13.43.13.0", {"start": v(9.08, -25.97) * mm, "end": v(8.85, -26.06) * mm});
            skArc(sketch, "E13.46.13.0", {"start": v(9.08, -25.97) * mm, "mid": v(9.28, -25.85) * mm, "end": v(9.4, -25.66) * mm});
            skPoint(sketch, "E13.4.14.0", {"position": v(15.7, -22.6) * mm});
            skPoint(sketch, "E13.5.14.0", {"position": v(14.88, -23.15) * mm});
            skArc(sketch, "E13.6.14.0", {"start": v(15.37, -17.5) * mm, "mid": v(14.83, -18.49) * mm, "end": v(15.1, -19.58) * mm});
            skPoint(sketch, "E13.10.14.0", {"position": v(11.52, -20.24) * mm});
            skPoint(sketch, "E13.11.14.0", {"position": v(14.29, -18.38) * mm});
            skPoint(sketch, "E13.12.14.0", {"position": v(15.47, -20.15) * mm});
            skArc(sketch, "E13.13.14.0", {"start": v(12.32, -21.44) * mm, "mid": v(11.4, -20.78) * mm, "end": v(10.28, -20.9) * mm});
            skPoint(sketch, "E13.17.14.0", {"position": v(12.7, -22) * mm});
            skArc(sketch, "E13.18.14.0", {"start": v(12.93, -22.18) * mm, "mid": v(13.75, -22.7) * mm, "end": v(14.64, -23.07) * mm});
            skArc(sketch, "E13.19.14.0", {"start": v(15.55, -20.44) * mm, "mid": v(15.7, -21.4) * mm, "end": v(15.71, -22.35) * mm});
            skLineSegment(sketch, "E13.22.14.0", {"start": v(15.32, -19.93) * mm, "end": v(15.1, -19.58) * mm});
            skArc(sketch, "E13.25.14.0", {"start": v(14.64, -23.07) * mm, "mid": v(14.86, -23.1) * mm, "end": v(15.08, -23.02) * mm});
            skArc(sketch, "E13.29.14.0", {"start": v(12.55, -21.78) * mm, "mid": v(12.72, -22) * mm, "end": v(12.93, -22.18) * mm});
            skLineSegment(sketch, "E13.33.14.0", {"start": v(12.55, -21.78) * mm, "end": v(12.32, -21.44) * mm});
            skLineSegment(sketch, "E13.36.14.0", {"start": v(15.08, -23.02) * mm, "end": v(15.29, -22.88) * mm});
            skArc(sketch, "E13.39.14.0", {"start": v(15.55, -20.44) * mm, "mid": v(15.46, -20.18) * mm, "end": v(15.32, -19.93) * mm});
            skLineSegment(sketch, "E13.43.14.0", {"start": v(15.5, -22.74) * mm, "end": v(15.29, -22.88) * mm});
            skArc(sketch, "E13.46.14.0", {"start": v(15.5, -22.74) * mm, "mid": v(15.65, -22.57) * mm, "end": v(15.71, -22.35) * mm});
            skPoint(sketch, "E13.4.15.0", {"position": v(21, -17.77) * mm});
            skPoint(sketch, "E13.5.15.0", {"position": v(20.36, -18.51) * mm});
            skArc(sketch, "E13.6.15.0", {"start": v(19.37, -12.92) * mm, "mid": v(19.11, -14.02) * mm, "end": v(19.65, -15.01) * mm});
            skPoint(sketch, "E13.10.15.0", {"position": v(16.36, -16.57) * mm});
            skPoint(sketch, "E13.11.15.0", {"position": v(18.56, -14.06) * mm});
            skPoint(sketch, "E13.12.15.0", {"position": v(20.15, -15.46) * mm});
            skArc(sketch, "E13.13.15.0", {"start": v(17.45, -17.52) * mm, "mid": v(16.4, -17.12) * mm, "end": v(15.34, -17.52) * mm});
            skPoint(sketch, "E13.17.15.0", {"position": v(17.96, -17.96) * mm});
            skArc(sketch, "E13.18.15.0", {"start": v(18.24, -18.08) * mm, "mid": v(19.16, -18.36) * mm, "end": v(20.11, -18.5) * mm});
            skArc(sketch, "E13.19.15.0", {"start": v(20.3, -15.72) * mm, "mid": v(20.7, -16.6) * mm, "end": v(20.97, -17.52) * mm});
            skLineSegment(sketch, "E13.22.15.0", {"start": v(19.96, -15.29) * mm, "end": v(19.65, -15.01) * mm});
            skArc(sketch, "E13.25.15.0", {"start": v(20.11, -18.5) * mm, "mid": v(20.34, -18.46) * mm, "end": v(20.52, -18.33) * mm});
            skArc(sketch, "E13.29.15.0", {"start": v(17.76, -17.8) * mm, "mid": v(17.99, -17.96) * mm, "end": v(18.24, -18.08) * mm});
            skLineSegment(sketch, "E13.33.15.0", {"start": v(17.76, -17.8) * mm, "end": v(17.45, -17.52) * mm});
            skLineSegment(sketch, "E13.36.15.0", {"start": v(20.52, -18.33) * mm, "end": v(20.7, -18.15) * mm});
            skArc(sketch, "E13.39.15.0", {"start": v(20.3, -15.72) * mm, "mid": v(20.15, -15.49) * mm, "end": v(19.96, -15.29) * mm});
            skLineSegment(sketch, "E13.43.15.0", {"start": v(20.85, -17.95) * mm, "end": v(20.7, -18.15) * mm});
            skArc(sketch, "E13.46.15.0", {"start": v(20.85, -17.95) * mm, "mid": v(20.96, -17.75) * mm, "end": v(20.97, -17.52) * mm});
            skPoint(sketch, "E13.4.16.0", {"position": v(24.9, -11.73) * mm});
            skPoint(sketch, "E13.5.16.0", {"position": v(24.46, -12.6) * mm});
            skArc(sketch, "E13.6.16.0", {"start": v(22.05, -7.47) * mm, "mid": v(22.1, -8.6) * mm, "end": v(22.86, -9.42) * mm});
            skPoint(sketch, "E13.10.16.0", {"position": v(20.1, -11.77) * mm});
            skPoint(sketch, "E13.11.16.0", {"position": v(21.57, -8.78) * mm});
            skPoint(sketch, "E13.12.16.0", {"position": v(23.47, -9.71) * mm});
            skArc(sketch, "E13.13.16.0", {"start": v(21.39, -12.4) * mm, "mid": v(20.27, -12.3) * mm, "end": v(19.35, -12.95) * mm});
            skPoint(sketch, "E13.17.16.0", {"position": v(22, -12.7) * mm});
            skArc(sketch, "E13.18.16.0", {"start": v(22.3, -12.74) * mm, "mid": v(23.26, -12.78) * mm, "end": v(24.21, -12.66) * mm});
            skArc(sketch, "E13.19.16.0", {"start": v(23.68, -9.93) * mm, "mid": v(24.3, -10.67) * mm, "end": v(24.79, -11.5) * mm});
            skLineSegment(sketch, "E13.22.16.0", {"start": v(23.23, -9.6) * mm, "end": v(22.86, -9.42) * mm});
            skArc(sketch, "E13.25.16.0", {"start": v(24.21, -12.66) * mm, "mid": v(24.42, -12.57) * mm, "end": v(24.57, -12.4) * mm});
            skArc(sketch, "E13.29.16.0", {"start": v(21.76, -12.59) * mm, "mid": v(22.02, -12.7) * mm, "end": v(22.3, -12.74) * mm});
            skLineSegment(sketch, "E13.33.16.0", {"start": v(21.76, -12.59) * mm, "end": v(21.39, -12.4) * mm});
            skLineSegment(sketch, "E13.36.16.0", {"start": v(24.57, -12.4) * mm, "end": v(24.68, -12.17) * mm});
            skArc(sketch, "E13.39.16.0", {"start": v(23.68, -9.93) * mm, "mid": v(23.47, -9.74) * mm, "end": v(23.23, -9.6) * mm});
            skLineSegment(sketch, "E13.43.16.0", {"start": v(24.8, -11.94) * mm, "end": v(24.68, -12.17) * mm});
            skArc(sketch, "E13.46.16.0", {"start": v(24.8, -11.94) * mm, "mid": v(24.84, -11.72) * mm, "end": v(24.79, -11.5) * mm});
            skPoint(sketch, "E13.4.17.0", {"position": v(27.08, -4.88) * mm});
            skPoint(sketch, "E13.5.17.0", {"position": v(26.89, -5.85) * mm});
            skArc(sketch, "E13.6.17.0", {"start": v(23.23, -1.5) * mm, "mid": v(23.56, -2.58) * mm, "end": v(24.52, -3.18) * mm});
            skPoint(sketch, "E13.10.17.0", {"position": v(22.45, -6.17) * mm});
            skPoint(sketch, "E13.11.17.0", {"position": v(23.1, -2.9) * mm});
            skPoint(sketch, "E13.12.17.0", {"position": v(25.18, -3.3) * mm});
            skArc(sketch, "E13.13.17.0", {"start": v(23.87, -6.45) * mm, "mid": v(22.76, -6.63) * mm, "end": v(22.04, -7.5) * mm});
            skPoint(sketch, "E13.17.17.0", {"position": v(24.53, -6.58) * mm});
            skArc(sketch, "E13.18.17.0", {"start": v(24.83, -6.54) * mm, "mid": v(25.77, -6.32) * mm, "end": v(26.67, -5.96) * mm});
            skArc(sketch, "E13.19.17.0", {"start": v(25.45, -3.46) * mm, "mid": v(26.23, -4.02) * mm, "end": v(26.92, -4.7) * mm});
            skLineSegment(sketch, "E13.22.17.0", {"start": v(24.93, -3.26) * mm, "end": v(24.52, -3.18) * mm});
            skArc(sketch, "E13.25.17.0", {"start": v(26.67, -5.96) * mm, "mid": v(26.84, -5.82) * mm, "end": v(26.94, -5.62) * mm});
            skArc(sketch, "E13.29.17.0", {"start": v(24.28, -6.53) * mm, "mid": v(24.55, -6.56) * mm, "end": v(24.83, -6.54) * mm});
            skLineSegment(sketch, "E13.33.17.0", {"start": v(24.28, -6.53) * mm, "end": v(23.87, -6.45) * mm});
            skLineSegment(sketch, "E13.36.17.0", {"start": v(26.94, -5.62) * mm, "end": v(27, -5.37) * mm});
            skArc(sketch, "E13.39.17.0", {"start": v(25.45, -3.46) * mm, "mid": v(25.2, -3.34) * mm, "end": v(24.93, -3.26) * mm});
            skLineSegment(sketch, "E13.43.17.0", {"start": v(27.04, -5.12) * mm, "end": v(27, -5.37) * mm});
            skArc(sketch, "E13.46.17.0", {"start": v(27.04, -5.12) * mm, "mid": v(27.03, -4.9) * mm, "end": v(26.92, -4.7) * mm});
            skPoint(sketch, "E13.4.18.0", {"position": v(27.42, 2.3) * mm});
            skPoint(sketch, "E13.5.18.0", {"position": v(27.49, 1.3) * mm});
            skArc(sketch, "E13.6.18.0", {"start": v(22.83, 4.56) * mm, "mid": v(23.43, 3.6) * mm, "end": v(24.5, 3.28) * mm});
            skPoint(sketch, "E13.10.18.0", {"position": v(23.28, -0.14) * mm});
            skPoint(sketch, "E13.11.18.0", {"position": v(23.06, 3.18) * mm});
            skPoint(sketch, "E13.12.18.0", {"position": v(25.18, 3.32) * mm});
            skArc(sketch, "E13.13.18.0", {"start": v(24.72, -0.05) * mm, "mid": v(23.7, -0.51) * mm, "end": v(23.23, -1.54) * mm});
            skPoint(sketch, "E13.17.18.0", {"position": v(25.4, 0) * mm});
            skArc(sketch, "E13.18.18.0", {"start": v(25.68, 0.1) * mm, "mid": v(26.53, 0.56) * mm, "end": v(27.3, 1.14) * mm});
            skArc(sketch, "E13.19.18.0", {"start": v(25.47, 3.24) * mm, "mid": v(26.38, 2.9) * mm, "end": v(27.22, 2.43) * mm});
            skLineSegment(sketch, "E13.22.18.0", {"start": v(24.92, 3.3) * mm, "end": v(24.5, 3.28) * mm});
            skArc(sketch, "E13.25.18.0", {"start": v(27.3, 1.14) * mm, "mid": v(27.43, 1.32) * mm, "end": v(27.47, 1.55) * mm});
            skArc(sketch, "E13.29.18.0", {"start": v(25.14, -0.02) * mm, "mid": v(25.42, 0.02) * mm, "end": v(25.68, 0.1) * mm});
            skLineSegment(sketch, "E13.33.18.0", {"start": v(25.14, -0.02) * mm, "end": v(24.72, -0.05) * mm});
            skLineSegment(sketch, "E13.36.18.0", {"start": v(27.47, 1.55) * mm, "end": v(27.46, 1.8) * mm});
            skArc(sketch, "E13.39.18.0", {"start": v(25.47, 3.24) * mm, "mid": v(25.2, 3.3) * mm, "end": v(24.92, 3.3) * mm});
            skLineSegment(sketch, "E13.43.18.0", {"start": v(27.44, 2.05) * mm, "end": v(27.46, 1.8) * mm});
            skArc(sketch, "E13.46.18.0", {"start": v(27.44, 2.05) * mm, "mid": v(27.37, 2.27) * mm, "end": v(27.22, 2.43) * mm});
            skPoint(sketch, "E13.4.19.0", {"position": v(25.9, 9.3) * mm});
            skPoint(sketch, "E13.5.19.0", {"position": v(26.21, 8.38) * mm});
            skArc(sketch, "E13.6.19.0", {"start": v(20.87, 10.31) * mm, "mid": v(21.7, 9.54) * mm, "end": v(22.82, 9.5) * mm});
            skPoint(sketch, "E13.10.19.0", {"position": v(22.53, 5.89) * mm});
            skPoint(sketch, "E13.11.19.0", {"position": v(21.46, 9.04) * mm});
            skPoint(sketch, "E13.12.19.0", {"position": v(23.46, 9.73) * mm});
            skArc(sketch, "E13.13.19.0", {"start": v(23.9, 6.35) * mm, "mid": v(23.02, 5.64) * mm, "end": v(22.84, 4.52) * mm});
            skPoint(sketch, "E13.17.19.0", {"position": v(24.54, 6.57) * mm});
            skArc(sketch, "E13.18.19.0", {"start": v(24.78, 6.75) * mm, "mid": v(25.48, 7.41) * mm, "end": v(26.08, 8.17) * mm});
            skArc(sketch, "E13.19.19.0", {"start": v(23.77, 9.73) * mm, "mid": v(24.73, 9.63) * mm, "end": v(25.66, 9.4) * mm});
            skLineSegment(sketch, "E13.22.19.0", {"start": v(23.22, 9.64) * mm, "end": v(22.82, 9.5) * mm});
            skArc(sketch, "E13.25.19.0", {"start": v(26.08, 8.17) * mm, "mid": v(26.16, 8.38) * mm, "end": v(26.14, 8.6) * mm});
            skArc(sketch, "E13.29.19.0", {"start": v(24.29, 6.48) * mm, "mid": v(24.54, 6.6) * mm, "end": v(24.78, 6.75) * mm});
            skLineSegment(sketch, "E13.33.19.0", {"start": v(24.29, 6.48) * mm, "end": v(23.9, 6.35) * mm});
            skLineSegment(sketch, "E13.36.19.0", {"start": v(26.14, 8.6) * mm, "end": v(26.06, 8.85) * mm});
            skArc(sketch, "E13.39.19.0", {"start": v(23.77, 9.73) * mm, "mid": v(23.49, 9.7) * mm, "end": v(23.22, 9.64) * mm});
            skLineSegment(sketch, "E13.43.19.0", {"start": v(25.97, 9.08) * mm, "end": v(26.06, 8.85) * mm});
            skArc(sketch, "E13.46.19.0", {"start": v(25.97, 9.08) * mm, "mid": v(25.85, 9.28) * mm, "end": v(25.66, 9.4) * mm});
            skPoint(sketch, "E13.4.20.0", {"position": v(22.6, 15.7) * mm});
            skPoint(sketch, "E13.5.20.0", {"position": v(23.15, 14.88) * mm});
            skArc(sketch, "E13.6.20.0", {"start": v(17.5, 15.37) * mm, "mid": v(18.49, 14.83) * mm, "end": v(19.58, 15.1) * mm});
            skPoint(sketch, "E13.10.20.0", {"position": v(20.24, 11.52) * mm});
            skPoint(sketch, "E13.11.20.0", {"position": v(18.38, 14.29) * mm});
            skPoint(sketch, "E13.12.20.0", {"position": v(20.15, 15.47) * mm});
            skArc(sketch, "E13.13.20.0", {"start": v(21.44, 12.32) * mm, "mid": v(20.78, 11.4) * mm, "end": v(20.9, 10.28) * mm});
            skPoint(sketch, "E13.17.20.0", {"position": v(22, 12.7) * mm});
            skArc(sketch, "E13.18.20.0", {"start": v(22.18, 12.93) * mm, "mid": v(22.7, 13.75) * mm, "end": v(23.07, 14.64) * mm});
            skArc(sketch, "E13.19.20.0", {"start": v(20.44, 15.55) * mm, "mid": v(21.4, 15.7) * mm, "end": v(22.35, 15.71) * mm});
            skLineSegment(sketch, "E13.22.20.0", {"start": v(19.93, 15.32) * mm, "end": v(19.58, 15.1) * mm});
            skArc(sketch, "E13.25.20.0", {"start": v(23.07, 14.64) * mm, "mid": v(23.1, 14.86) * mm, "end": v(23.02, 15.08) * mm});
            skArc(sketch, "E13.29.20.0", {"start": v(21.78, 12.55) * mm, "mid": v(22, 12.72) * mm, "end": v(22.18, 12.93) * mm});
            skLineSegment(sketch, "E13.33.20.0", {"start": v(21.78, 12.55) * mm, "end": v(21.44, 12.32) * mm});
            skLineSegment(sketch, "E13.36.20.0", {"start": v(23.02, 15.08) * mm, "end": v(22.88, 15.29) * mm});
            skArc(sketch, "E13.39.20.0", {"start": v(20.44, 15.55) * mm, "mid": v(20.18, 15.46) * mm, "end": v(19.93, 15.32) * mm});
            skLineSegment(sketch, "E13.43.20.0", {"start": v(22.74, 15.5) * mm, "end": v(22.88, 15.29) * mm});
            skArc(sketch, "E13.46.20.0", {"start": v(22.74, 15.5) * mm, "mid": v(22.57, 15.65) * mm, "end": v(22.35, 15.71) * mm});
            skPoint(sketch, "E13.4.21.0", {"position": v(17.77, 21) * mm});
            skPoint(sketch, "E13.5.21.0", {"position": v(18.51, 20.36) * mm});
            skArc(sketch, "E13.6.21.0", {"start": v(12.92, 19.37) * mm, "mid": v(14.02, 19.11) * mm, "end": v(15.01, 19.65) * mm});
            skPoint(sketch, "E13.10.21.0", {"position": v(16.57, 16.36) * mm});
            skPoint(sketch, "E13.11.21.0", {"position": v(14.06, 18.56) * mm});
            skPoint(sketch, "E13.12.21.0", {"position": v(15.46, 20.15) * mm});
            skArc(sketch, "E13.13.21.0", {"start": v(17.52, 17.45) * mm, "mid": v(17.12, 16.4) * mm, "end": v(17.52, 15.34) * mm});
            skPoint(sketch, "E13.17.21.0", {"position": v(17.96, 17.96) * mm});
            skArc(sketch, "E13.18.21.0", {"start": v(18.08, 18.24) * mm, "mid": v(18.36, 19.16) * mm, "end": v(18.5, 20.11) * mm});
            skArc(sketch, "E13.19.21.0", {"start": v(15.72, 20.3) * mm, "mid": v(16.6, 20.7) * mm, "end": v(17.52, 20.97) * mm});
            skLineSegment(sketch, "E13.22.21.0", {"start": v(15.29, 19.96) * mm, "end": v(15.01, 19.65) * mm});
            skArc(sketch, "E13.25.21.0", {"start": v(18.5, 20.11) * mm, "mid": v(18.46, 20.34) * mm, "end": v(18.33, 20.52) * mm});
            skArc(sketch, "E13.29.21.0", {"start": v(17.8, 17.76) * mm, "mid": v(17.96, 17.99) * mm, "end": v(18.08, 18.24) * mm});
            skLineSegment(sketch, "E13.33.21.0", {"start": v(17.8, 17.76) * mm, "end": v(17.52, 17.45) * mm});
            skLineSegment(sketch, "E13.36.21.0", {"start": v(18.33, 20.52) * mm, "end": v(18.15, 20.7) * mm});
            skArc(sketch, "E13.39.21.0", {"start": v(15.72, 20.3) * mm, "mid": v(15.49, 20.15) * mm, "end": v(15.29, 19.96) * mm});
            skLineSegment(sketch, "E13.43.21.0", {"start": v(17.95, 20.85) * mm, "end": v(18.15, 20.7) * mm});
            skArc(sketch, "E13.46.21.0", {"start": v(17.95, 20.85) * mm, "mid": v(17.75, 20.96) * mm, "end": v(17.52, 20.97) * mm});
            skPoint(sketch, "E13.4.22.0", {"position": v(11.73, 24.9) * mm});
            skPoint(sketch, "E13.5.22.0", {"position": v(12.6, 24.46) * mm});
            skArc(sketch, "E13.6.22.0", {"start": v(7.47, 22.05) * mm, "mid": v(8.6, 22.1) * mm, "end": v(9.42, 22.86) * mm});
            skPoint(sketch, "E13.10.22.0", {"position": v(11.77, 20.1) * mm});
            skPoint(sketch, "E13.11.22.0", {"position": v(8.78, 21.57) * mm});
            skPoint(sketch, "E13.12.22.0", {"position": v(9.71, 23.47) * mm});
            skArc(sketch, "E13.13.22.0", {"start": v(12.4, 21.39) * mm, "mid": v(12.3, 20.27) * mm, "end": v(12.95, 19.35) * mm});
            skPoint(sketch, "E13.17.22.0", {"position": v(12.7, 22) * mm});
            skArc(sketch, "E13.18.22.0", {"start": v(12.74, 22.3) * mm, "mid": v(12.78, 23.26) * mm, "end": v(12.66, 24.21) * mm});
            skArc(sketch, "E13.19.22.0", {"start": v(9.93, 23.68) * mm, "mid": v(10.67, 24.3) * mm, "end": v(11.5, 24.79) * mm});
            skLineSegment(sketch, "E13.22.22.0", {"start": v(9.6, 23.23) * mm, "end": v(9.42, 22.86) * mm});
            skArc(sketch, "E13.25.22.0", {"start": v(12.66, 24.21) * mm, "mid": v(12.57, 24.42) * mm, "end": v(12.4, 24.57) * mm});
            skArc(sketch, "E13.29.22.0", {"start": v(12.59, 21.76) * mm, "mid": v(12.7, 22.02) * mm, "end": v(12.74, 22.3) * mm});
            skLineSegment(sketch, "E13.33.22.0", {"start": v(12.59, 21.76) * mm, "end": v(12.4, 21.39) * mm});
            skLineSegment(sketch, "E13.36.22.0", {"start": v(12.4, 24.57) * mm, "end": v(12.17, 24.68) * mm});
            skArc(sketch, "E13.39.22.0", {"start": v(9.93, 23.68) * mm, "mid": v(9.74, 23.47) * mm, "end": v(9.6, 23.23) * mm});
            skLineSegment(sketch, "E13.43.22.0", {"start": v(11.94, 24.8) * mm, "end": v(12.17, 24.68) * mm});
            skArc(sketch, "E13.46.22.0", {"start": v(11.94, 24.8) * mm, "mid": v(11.72, 24.84) * mm, "end": v(11.5, 24.79) * mm});
            skPoint(sketch, "E13.4.23.0", {"position": v(4.88, 27.08) * mm});
            skPoint(sketch, "E13.5.23.0", {"position": v(5.85, 26.89) * mm});
            skArc(sketch, "E13.6.23.0", {"start": v(1.5, 23.23) * mm, "mid": v(2.58, 23.56) * mm, "end": v(3.18, 24.52) * mm});
            skPoint(sketch, "E13.10.23.0", {"position": v(6.17, 22.45) * mm});
            skPoint(sketch, "E13.11.23.0", {"position": v(2.9, 23.1) * mm});
            skPoint(sketch, "E13.12.23.0", {"position": v(3.3, 25.18) * mm});
            skArc(sketch, "E13.13.23.0", {"start": v(6.45, 23.87) * mm, "mid": v(6.63, 22.76) * mm, "end": v(7.5, 22.04) * mm});
            skPoint(sketch, "E13.17.23.0", {"position": v(6.58, 24.53) * mm});
            skArc(sketch, "E13.18.23.0", {"start": v(6.54, 24.83) * mm, "mid": v(6.32, 25.77) * mm, "end": v(5.96, 26.67) * mm});
            skArc(sketch, "E13.19.23.0", {"start": v(3.46, 25.45) * mm, "mid": v(4.02, 26.23) * mm, "end": v(4.7, 26.92) * mm});
            skLineSegment(sketch, "E13.22.23.0", {"start": v(3.26, 24.93) * mm, "end": v(3.18, 24.52) * mm});
            skArc(sketch, "E13.25.23.0", {"start": v(5.96, 26.67) * mm, "mid": v(5.82, 26.84) * mm, "end": v(5.62, 26.94) * mm});
            skArc(sketch, "E13.29.23.0", {"start": v(6.53, 24.28) * mm, "mid": v(6.56, 24.55) * mm, "end": v(6.54, 24.83) * mm});
            skLineSegment(sketch, "E13.33.23.0", {"start": v(6.53, 24.28) * mm, "end": v(6.45, 23.87) * mm});
            skLineSegment(sketch, "E13.36.23.0", {"start": v(5.62, 26.94) * mm, "end": v(5.37, 27) * mm});
            skArc(sketch, "E13.39.23.0", {"start": v(3.46, 25.45) * mm, "mid": v(3.34, 25.2) * mm, "end": v(3.26, 24.93) * mm});
            skLineSegment(sketch, "E13.43.23.0", {"start": v(5.12, 27.04) * mm, "end": v(5.37, 27) * mm});
            skArc(sketch, "E13.46.23.0", {"start": v(5.12, 27.04) * mm, "mid": v(4.9, 27.03) * mm, "end": v(4.7, 26.92) * mm});
            skSolve(sketch);
        }
        {
            var Q0;
            Q0 = qSketchRegion(id + "F0", true);
            extrude(context, id + "F1", {"entities" : qUnion([Q0]), "depth" : 6.35 * mm});
        }
        {
            var Q0;
            Q0=makeQuery(id+"F1.opExtrude","CAP_FACE",FACE,{"disambiguationData":[OSD([sQuery(id+"F0.wireOp",EDGE,"E0.trimOffspring"),sQuery(id+"F0.wireOp",EDGE,"E1"),sQuery(id+"F0.wireOp",EDGE,"E2.MirrorCS"),sQuery(id+"F0.wireOp",EDGE,"E3.MirrorCS"),sQuery(id+"F0.wireOp",EDGE,"E4"),sQuery(id+"F0.wireOp",EDGE,"E5.MirrorCS"),sQuery(id+"F0.wireOp",EDGE,"E6.filletArc"),sQuery(id+"F0.wireOp",EDGE,"E7.filletArc"),sQuery(id+"F0.wireOp",EDGE,"E8.filletArc"),sQuery(id+"F0.wireOp",EDGE,"E9.filletArc"),sQuery(id+"F0.wireOp",EDGE,"E10.filletArc"),sQuery(id+"F0.wireOp",EDGE,"E11.filletArc"),sQuery(id+"F0.wireOp",EDGE,"E12.1.0"),sQuery(id+"F0.wireOp",EDGE,"E12.1.3"),sQuery(id+"F0.wireOp",EDGE,"E12.1.7"),sQuery(id+"F0.wireOp",EDGE,"E12.1.9"),sQuery(id+"F0.wireOp",EDGE,"E12.1.10"),sQuery(id+"F0.wireOp",EDGE,"E12.1.11"),sQuery(id+"F0.wireOp",EDGE,"E12.1.12"),sQuery(id+"F0.wireOp",EDGE,"E12.1.13"),sQuery(id+"F0.wireOp",EDGE,"E12.1.14"),sQuery(id+"F0.wireOp",EDGE,"E12.1.15"),sQuery(id+"F0.wireOp",EDGE,"E12.1.16"),sQuery(id+"F0.wireOp",EDGE,"E12.1.17"),sQuery(id+"F0.wireOp",EDGE,"E12.2.0"),sQuery(id+"F0.wireOp",EDGE,"E12.2.3"),sQuery(id+"F0.wireOp",EDGE,"E12.2.7"),sQuery(id+"F0.wireOp",EDGE,"E12.2.9"),sQuery(id+"F0.wireOp",EDGE,"E12.2.10"),sQuery(id+"F0.wireOp",EDGE,"E12.2.11"),sQuery(id+"F0.wireOp",EDGE,"E12.2.12"),sQuery(id+"F0.wireOp",EDGE,"E12.2.13"),sQuery(id+"F0.wireOp",EDGE,"E12.2.14"),sQuery(id+"F0.wireOp",EDGE,"E12.2.15"),sQuery(id+"F0.wireOp",EDGE,"E12.2.16"),sQuery(id+"F0.wireOp",EDGE,"E12.2.17"),sQuery(id+"F0.wireOp",EDGE,"E13.6.3.0"),sQuery(id+"F0.wireOp",EDGE,"E13.13.3.0"),sQuery(id+"F0.wireOp",EDGE,"E13.18.3.0"),sQuery(id+"F0.wireOp",EDGE,"E13.19.3.0"),sQuery(id+"F0.wireOp",EDGE,"E13.22.3.0"),sQuery(id+"F0.wireOp",EDGE,"E13.25.3.0"),sQuery(id+"F0.wireOp",EDGE,"E13.29.3.0"),sQuery(id+"F0.wireOp",EDGE,"E13.33.3.0"),sQuery(id+"F0.wireOp",EDGE,"E13.36.3.0"),sQuery(id+"F0.wireOp",EDGE,"E13.39.3.0"),sQuery(id+"F0.wireOp",EDGE,"E13.43.3.0"),sQuery(id+"F0.wireOp",EDGE,"E13.46.3.0"),sQuery(id+"F0.wireOp",EDGE,"E13.6.4.0"),sQuery(id+"F0.wireOp",EDGE,"E13.13.4.0"),sQuery(id+"F0.wireOp",EDGE,"E13.18.4.0"),sQuery(id+"F0.wireOp",EDGE,"E13.19.4.0"),sQuery(id+"F0.wireOp",EDGE,"E13.22.4.0"),sQuery(id+"F0.wireOp",EDGE,"E13.25.4.0"),sQuery(id+"F0.wireOp",EDGE,"E13.29.4.0"),sQuery(id+"F0.wireOp",EDGE,"E13.33.4.0"),sQuery(id+"F0.wireOp",EDGE,"E13.36.4.0"),sQuery(id+"F0.wireOp",EDGE,"E13.39.4.0"),sQuery(id+"F0.wireOp",EDGE,"E13.43.4.0"),sQuery(id+"F0.wireOp",EDGE,"E13.46.4.0"),sQuery(id+"F0.wireOp",EDGE,"E13.6.5.0"),sQuery(id+"F0.wireOp",EDGE,"E13.13.5.0"),sQuery(id+"F0.wireOp",EDGE,"E13.18.5.0"),sQuery(id+"F0.wireOp",EDGE,"E13.19.5.0"),sQuery(id+"F0.wireOp",EDGE,"E13.22.5.0"),sQuery(id+"F0.wireOp",EDGE,"E13.25.5.0"),sQuery(id+"F0.wireOp",EDGE,"E13.29.5.0"),sQuery(id+"F0.wireOp",EDGE,"E13.33.5.0"),sQuery(id+"F0.wireOp",EDGE,"E13.36.5.0"),sQuery(id+"F0.wireOp",EDGE,"E13.39.5.0"),sQuery(id+"F0.wireOp",EDGE,"E13.43.5.0"),sQuery(id+"F0.wireOp",EDGE,"E13.46.5.0"),sQuery(id+"F0.wireOp",EDGE,"E13.6.6.0"),sQuery(id+"F0.wireOp",EDGE,"E13.13.6.0"),sQuery(id+"F0.wireOp",EDGE,"E13.18.6.0"),sQuery(id+"F0.wireOp",EDGE,"E13.19.6.0"),sQuery(id+"F0.wireOp",EDGE,"E13.22.6.0"),sQuery(id+"F0.wireOp",EDGE,"E13.25.6.0"),sQuery(id+"F0.wireOp",EDGE,"E13.29.6.0"),sQuery(id+"F0.wireOp",EDGE,"E13.33.6.0"),sQuery(id+"F0.wireOp",EDGE,"E13.36.6.0"),sQuery(id+"F0.wireOp",EDGE,"E13.39.6.0"),sQuery(id+"F0.wireOp",EDGE,"E13.43.6.0"),sQuery(id+"F0.wireOp",EDGE,"E13.46.6.0"),sQuery(id+"F0.wireOp",EDGE,"E13.6.7.0"),sQuery(id+"F0.wireOp",EDGE,"E13.13.7.0"),sQuery(id+"F0.wireOp",EDGE,"E13.18.7.0"),sQuery(id+"F0.wireOp",EDGE,"E13.19.7.0"),sQuery(id+"F0.wireOp",EDGE,"E13.22.7.0"),sQuery(id+"F0.wireOp",EDGE,"E13.25.7.0"),sQuery(id+"F0.wireOp",EDGE,"E13.29.7.0"),sQuery(id+"F0.wireOp",EDGE,"E13.33.7.0"),sQuery(id+"F0.wireOp",EDGE,"E13.36.7.0"),sQuery(id+"F0.wireOp",EDGE,"E13.39.7.0"),sQuery(id+"F0.wireOp",EDGE,"E13.43.7.0"),sQuery(id+"F0.wireOp",EDGE,"E13.46.7.0"),sQuery(id+"F0.wireOp",EDGE,"E13.6.8.0"),sQuery(id+"F0.wireOp",EDGE,"E13.13.8.0"),sQuery(id+"F0.wireOp",EDGE,"E13.18.8.0"),sQuery(id+"F0.wireOp",EDGE,"E13.19.8.0"),sQuery(id+"F0.wireOp",EDGE,"E13.22.8.0"),sQuery(id+"F0.wireOp",EDGE,"E13.25.8.0"),sQuery(id+"F0.wireOp",EDGE,"E13.29.8.0"),sQuery(id+"F0.wireOp",EDGE,"E13.33.8.0"),sQuery(id+"F0.wireOp",EDGE,"E13.36.8.0"),sQuery(id+"F0.wireOp",EDGE,"E13.39.8.0"),sQuery(id+"F0.wireOp",EDGE,"E13.43.8.0"),sQuery(id+"F0.wireOp",EDGE,"E13.46.8.0"),sQuery(id+"F0.wireOp",EDGE,"E13.6.9.0"),sQuery(id+"F0.wireOp",EDGE,"E13.13.9.0"),sQuery(id+"F0.wireOp",EDGE,"E13.18.9.0"),sQuery(id+"F0.wireOp",EDGE,"E13.19.9.0"),sQuery(id+"F0.wireOp",EDGE,"E13.22.9.0"),sQuery(id+"F0.wireOp",EDGE,"E13.25.9.0"),sQuery(id+"F0.wireOp",EDGE,"E13.29.9.0"),sQuery(id+"F0.wireOp",EDGE,"E13.33.9.0"),sQuery(id+"F0.wireOp",EDGE,"E13.36.9.0"),sQuery(id+"F0.wireOp",EDGE,"E13.39.9.0"),sQuery(id+"F0.wireOp",EDGE,"E13.43.9.0"),sQuery(id+"F0.wireOp",EDGE,"E13.46.9.0"),sQuery(id+"F0.wireOp",EDGE,"E13.6.10.0"),sQuery(id+"F0.wireOp",EDGE,"E13.13.10.0"),sQuery(id+"F0.wireOp",EDGE,"E13.18.10.0"),sQuery(id+"F0.wireOp",EDGE,"E13.19.10.0"),sQuery(id+"F0.wireOp",EDGE,"E13.22.10.0"),sQuery(id+"F0.wireOp",EDGE,"E13.25.10.0"),sQuery(id+"F0.wireOp",EDGE,"E13.29.10.0"),sQuery(id+"F0.wireOp",EDGE,"E13.33.10.0"),sQuery(id+"F0.wireOp",EDGE,"E13.36.10.0"),sQuery(id+"F0.wireOp",EDGE,"E13.39.10.0"),sQuery(id+"F0.wireOp",EDGE,"E13.43.10.0"),sQuery(id+"F0.wireOp",EDGE,"E13.46.10.0"),sQuery(id+"F0.wireOp",EDGE,"E13.6.11.0"),sQuery(id+"F0.wireOp",EDGE,"E13.13.11.0"),sQuery(id+"F0.wireOp",EDGE,"E13.18.11.0"),sQuery(id+"F0.wireOp",EDGE,"E13.19.11.0"),sQuery(id+"F0.wireOp",EDGE,"E13.22.11.0"),sQuery(id+"F0.wireOp",EDGE,"E13.25.11.0"),sQuery(id+"F0.wireOp",EDGE,"E13.29.11.0"),sQuery(id+"F0.wireOp",EDGE,"E13.33.11.0"),sQuery(id+"F0.wireOp",EDGE,"E13.36.11.0"),sQuery(id+"F0.wireOp",EDGE,"E13.39.11.0"),sQuery(id+"F0.wireOp",EDGE,"E13.43.11.0"),sQuery(id+"F0.wireOp",EDGE,"E13.46.11.0"),sQuery(id+"F0.wireOp",EDGE,"E13.6.12.0"),sQuery(id+"F0.wireOp",EDGE,"E13.13.12.0"),sQuery(id+"F0.wireOp",EDGE,"E13.18.12.0"),sQuery(id+"F0.wireOp",EDGE,"E13.19.12.0"),sQuery(id+"F0.wireOp",EDGE,"E13.22.12.0"),sQuery(id+"F0.wireOp",EDGE,"E13.25.12.0"),sQuery(id+"F0.wireOp",EDGE,"E13.29.12.0"),sQuery(id+"F0.wireOp",EDGE,"E13.33.12.0"),sQuery(id+"F0.wireOp",EDGE,"E13.36.12.0"),sQuery(id+"F0.wireOp",EDGE,"E13.39.12.0"),sQuery(id+"F0.wireOp",EDGE,"E13.43.12.0"),sQuery(id+"F0.wireOp",EDGE,"E13.46.12.0"),sQuery(id+"F0.wireOp",EDGE,"E13.6.13.0"),sQuery(id+"F0.wireOp",EDGE,"E13.13.13.0"),sQuery(id+"F0.wireOp",EDGE,"E13.18.13.0"),sQuery(id+"F0.wireOp",EDGE,"E13.19.13.0"),sQuery(id+"F0.wireOp",EDGE,"E13.22.13.0"),sQuery(id+"F0.wireOp",EDGE,"E13.25.13.0"),sQuery(id+"F0.wireOp",EDGE,"E13.29.13.0"),sQuery(id+"F0.wireOp",EDGE,"E13.33.13.0"),sQuery(id+"F0.wireOp",EDGE,"E13.36.13.0"),sQuery(id+"F0.wireOp",EDGE,"E13.39.13.0"),sQuery(id+"F0.wireOp",EDGE,"E13.43.13.0"),sQuery(id+"F0.wireOp",EDGE,"E13.46.13.0"),sQuery(id+"F0.wireOp",EDGE,"E13.6.14.0"),sQuery(id+"F0.wireOp",EDGE,"E13.13.14.0"),sQuery(id+"F0.wireOp",EDGE,"E13.18.14.0"),sQuery(id+"F0.wireOp",EDGE,"E13.19.14.0"),sQuery(id+"F0.wireOp",EDGE,"E13.22.14.0"),sQuery(id+"F0.wireOp",EDGE,"E13.25.14.0"),sQuery(id+"F0.wireOp",EDGE,"E13.29.14.0"),sQuery(id+"F0.wireOp",EDGE,"E13.33.14.0"),sQuery(id+"F0.wireOp",EDGE,"E13.36.14.0"),sQuery(id+"F0.wireOp",EDGE,"E13.39.14.0"),sQuery(id+"F0.wireOp",EDGE,"E13.43.14.0"),sQuery(id+"F0.wireOp",EDGE,"E13.46.14.0"),sQuery(id+"F0.wireOp",EDGE,"E13.6.15.0"),sQuery(id+"F0.wireOp",EDGE,"E13.13.15.0"),sQuery(id+"F0.wireOp",EDGE,"E13.18.15.0"),sQuery(id+"F0.wireOp",EDGE,"E13.19.15.0"),sQuery(id+"F0.wireOp",EDGE,"E13.22.15.0"),sQuery(id+"F0.wireOp",EDGE,"E13.25.15.0"),sQuery(id+"F0.wireOp",EDGE,"E13.29.15.0"),sQuery(id+"F0.wireOp",EDGE,"E13.33.15.0"),sQuery(id+"F0.wireOp",EDGE,"E13.36.15.0"),sQuery(id+"F0.wireOp",EDGE,"E13.39.15.0"),sQuery(id+"F0.wireOp",EDGE,"E13.43.15.0"),sQuery(id+"F0.wireOp",EDGE,"E13.46.15.0"),sQuery(id+"F0.wireOp",EDGE,"E13.6.16.0"),sQuery(id+"F0.wireOp",EDGE,"E13.13.16.0"),sQuery(id+"F0.wireOp",EDGE,"E13.18.16.0"),sQuery(id+"F0.wireOp",EDGE,"E13.19.16.0"),sQuery(id+"F0.wireOp",EDGE,"E13.22.16.0"),sQuery(id+"F0.wireOp",EDGE,"E13.25.16.0"),sQuery(id+"F0.wireOp",EDGE,"E13.29.16.0"),sQuery(id+"F0.wireOp",EDGE,"E13.33.16.0"),sQuery(id+"F0.wireOp",EDGE,"E13.36.16.0"),sQuery(id+"F0.wireOp",EDGE,"E13.39.16.0"),sQuery(id+"F0.wireOp",EDGE,"E13.43.16.0"),sQuery(id+"F0.wireOp",EDGE,"E13.46.16.0"),sQuery(id+"F0.wireOp",EDGE,"E13.6.17.0"),sQuery(id+"F0.wireOp",EDGE,"E13.13.17.0"),sQuery(id+"F0.wireOp",EDGE,"E13.18.17.0"),sQuery(id+"F0.wireOp",EDGE,"E13.19.17.0"),sQuery(id+"F0.wireOp",EDGE,"E13.22.17.0"),sQuery(id+"F0.wireOp",EDGE,"E13.25.17.0"),sQuery(id+"F0.wireOp",EDGE,"E13.29.17.0"),sQuery(id+"F0.wireOp",EDGE,"E13.33.17.0"),sQuery(id+"F0.wireOp",EDGE,"E13.36.17.0"),sQuery(id+"F0.wireOp",EDGE,"E13.39.17.0"),sQuery(id+"F0.wireOp",EDGE,"E13.43.17.0"),sQuery(id+"F0.wireOp",EDGE,"E13.46.17.0"),sQuery(id+"F0.wireOp",EDGE,"E13.6.18.0"),sQuery(id+"F0.wireOp",EDGE,"E13.13.18.0"),sQuery(id+"F0.wireOp",EDGE,"E13.18.18.0"),sQuery(id+"F0.wireOp",EDGE,"E13.19.18.0"),sQuery(id+"F0.wireOp",EDGE,"E13.22.18.0"),sQuery(id+"F0.wireOp",EDGE,"E13.25.18.0"),sQuery(id+"F0.wireOp",EDGE,"E13.29.18.0"),sQuery(id+"F0.wireOp",EDGE,"E13.33.18.0"),sQuery(id+"F0.wireOp",EDGE,"E13.36.18.0"),sQuery(id+"F0.wireOp",EDGE,"E13.39.18.0"),sQuery(id+"F0.wireOp",EDGE,"E13.43.18.0"),sQuery(id+"F0.wireOp",EDGE,"E13.46.18.0"),sQuery(id+"F0.wireOp",EDGE,"E13.6.19.0"),sQuery(id+"F0.wireOp",EDGE,"E13.13.19.0"),sQuery(id+"F0.wireOp",EDGE,"E13.18.19.0"),sQuery(id+"F0.wireOp",EDGE,"E13.19.19.0"),sQuery(id+"F0.wireOp",EDGE,"E13.22.19.0"),sQuery(id+"F0.wireOp",EDGE,"E13.25.19.0"),sQuery(id+"F0.wireOp",EDGE,"E13.29.19.0"),sQuery(id+"F0.wireOp",EDGE,"E13.33.19.0"),sQuery(id+"F0.wireOp",EDGE,"E13.36.19.0"),sQuery(id+"F0.wireOp",EDGE,"E13.39.19.0"),sQuery(id+"F0.wireOp",EDGE,"E13.43.19.0"),sQuery(id+"F0.wireOp",EDGE,"E13.46.19.0"),sQuery(id+"F0.wireOp",EDGE,"E13.6.20.0"),sQuery(id+"F0.wireOp",EDGE,"E13.13.20.0"),sQuery(id+"F0.wireOp",EDGE,"E13.18.20.0"),sQuery(id+"F0.wireOp",EDGE,"E13.19.20.0"),sQuery(id+"F0.wireOp",EDGE,"E13.22.20.0"),sQuery(id+"F0.wireOp",EDGE,"E13.25.20.0"),sQuery(id+"F0.wireOp",EDGE,"E13.29.20.0"),sQuery(id+"F0.wireOp",EDGE,"E13.33.20.0"),sQuery(id+"F0.wireOp",EDGE,"E13.36.20.0"),sQuery(id+"F0.wireOp",EDGE,"E13.39.20.0"),sQuery(id+"F0.wireOp",EDGE,"E13.43.20.0"),sQuery(id+"F0.wireOp",EDGE,"E13.46.20.0"),sQuery(id+"F0.wireOp",EDGE,"E13.6.21.0"),sQuery(id+"F0.wireOp",EDGE,"E13.13.21.0"),sQuery(id+"F0.wireOp",EDGE,"E13.18.21.0"),sQuery(id+"F0.wireOp",EDGE,"E13.19.21.0"),sQuery(id+"F0.wireOp",EDGE,"E13.22.21.0"),sQuery(id+"F0.wireOp",EDGE,"E13.25.21.0"),sQuery(id+"F0.wireOp",EDGE,"E13.29.21.0"),sQuery(id+"F0.wireOp",EDGE,"E13.33.21.0"),sQuery(id+"F0.wireOp",EDGE,"E13.36.21.0"),sQuery(id+"F0.wireOp",EDGE,"E13.39.21.0"),sQuery(id+"F0.wireOp",EDGE,"E13.43.21.0"),sQuery(id+"F0.wireOp",EDGE,"E13.46.21.0"),sQuery(id+"F0.wireOp",EDGE,"E13.6.22.0"),sQuery(id+"F0.wireOp",EDGE,"E13.13.22.0"),sQuery(id+"F0.wireOp",EDGE,"E13.18.22.0"),sQuery(id+"F0.wireOp",EDGE,"E13.19.22.0"),sQuery(id+"F0.wireOp",EDGE,"E13.22.22.0"),sQuery(id+"F0.wireOp",EDGE,"E13.25.22.0"),sQuery(id+"F0.wireOp",EDGE,"E13.29.22.0"),sQuery(id+"F0.wireOp",EDGE,"E13.33.22.0"),sQuery(id+"F0.wireOp",EDGE,"E13.36.22.0"),sQuery(id+"F0.wireOp",EDGE,"E13.39.22.0"),sQuery(id+"F0.wireOp",EDGE,"E13.43.22.0"),sQuery(id+"F0.wireOp",EDGE,"E13.46.22.0"),sQuery(id+"F0.wireOp",EDGE,"E13.6.23.0"),sQuery(id+"F0.wireOp",EDGE,"E13.13.23.0"),sQuery(id+"F0.wireOp",EDGE,"E13.18.23.0"),sQuery(id+"F0.wireOp",EDGE,"E13.19.23.0"),sQuery(id+"F0.wireOp",EDGE,"E13.22.23.0"),sQuery(id+"F0.wireOp",EDGE,"E13.25.23.0"),sQuery(id+"F0.wireOp",EDGE,"E13.29.23.0"),sQuery(id+"F0.wireOp",EDGE,"E13.33.23.0"),sQuery(id+"F0.wireOp",EDGE,"E13.36.23.0"),sQuery(id+"F0.wireOp",EDGE,"E13.39.23.0"),sQuery(id+"F0.wireOp",EDGE,"E13.43.23.0"),sQuery(id+"F0.wireOp",EDGE,"E13.46.23.0")])],"isStart":false});
            var sketch = newSketch(context, id + "F2", { "sketchPlane" : qUnion([Q0])});
            skCircle(sketch, "E14", {"center": v(0, 0) * mm, "radius": 6.35 * mm});
            skSolve(sketch);
        }
        {
            var Q0;
            Q0 = qSketchRegion(id + "F2", true);
            extrude(context, id + "F3", {"entities" : qUnion([Q0]), "operationType" : NewBodyOperationType.REMOVE, "oppositeDirection" : true, "depth" : 25.4 * mm});
        }
    });
